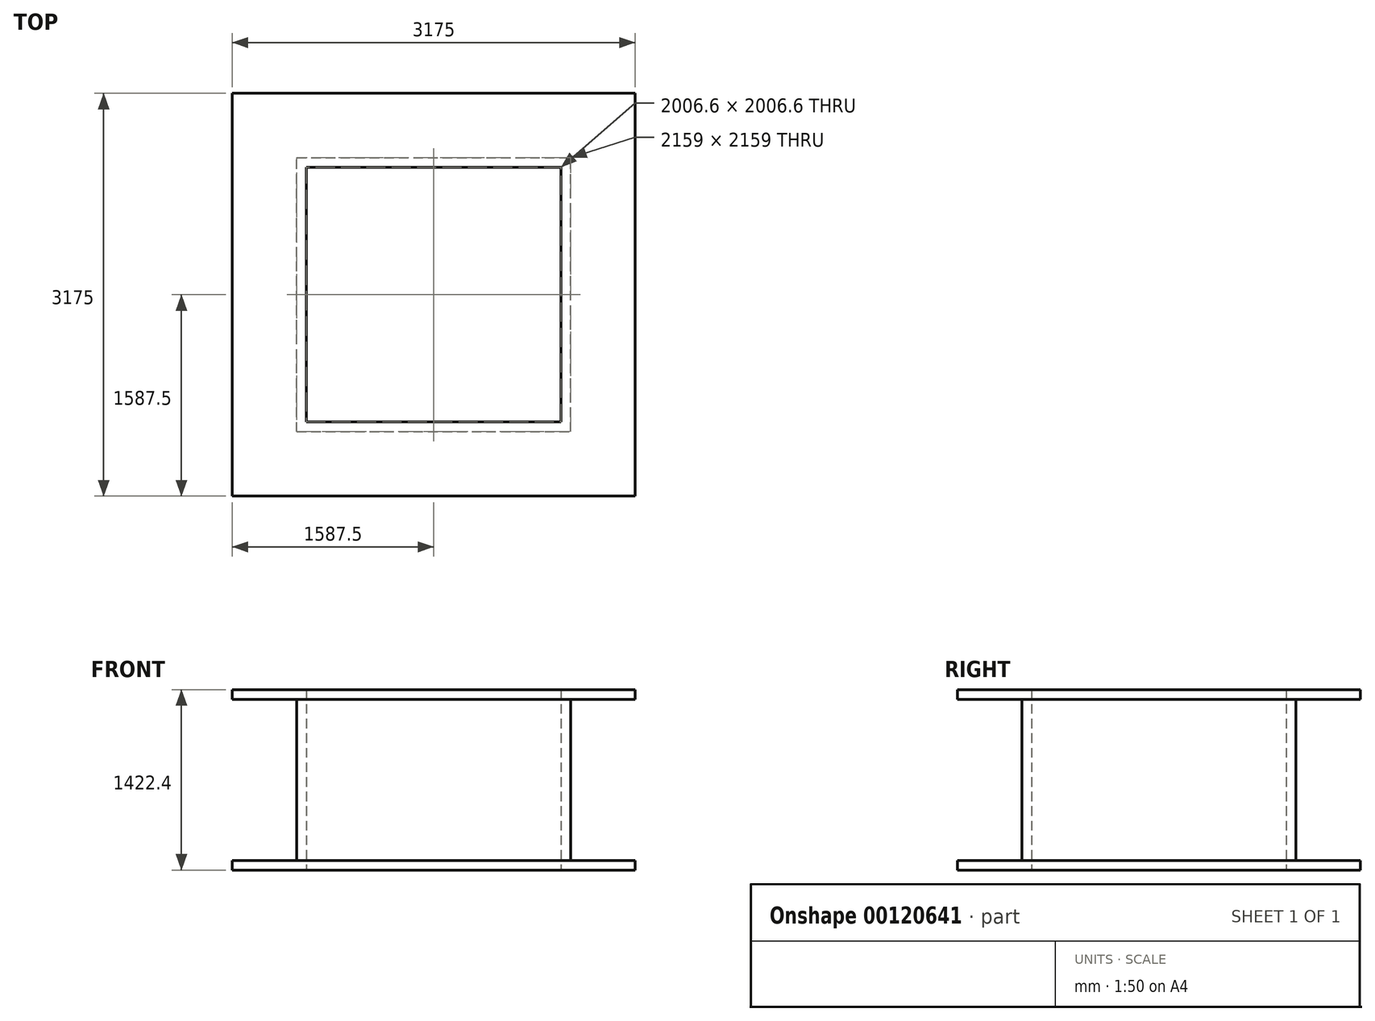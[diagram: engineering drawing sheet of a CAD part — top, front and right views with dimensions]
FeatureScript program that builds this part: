
annotation { "Feature Type Name" : "Feature", "Feature Type Description" : "" }
export const myFeature = defineFeature(function(context is Context, id is Id, definition is map)
    precondition{}
    {
        {
            var Q0;
            Q0=qCreatedBy(makeId("Top.planeOp"),FACE);
            var sketch = newSketch(context, id + "F0", { "sketchPlane" : qUnion([Q0])});
            skLineSegment(sketch, "E0.bottom", {"start": v(0, 0) * mm, "end": v(2159, 0) * mm});
            skLineSegment(sketch, "E0.top", {"start": v(0, 2159) * mm, "end": v(2159, 2159) * mm});
            skLineSegment(sketch, "E0.left", {"start": v(0, 0) * mm, "end": v(0, 2159) * mm});
            skLineSegment(sketch, "E0.right", {"start": v(2159, 0) * mm, "end": v(2159, 2159) * mm});
            skLineSegment(sketch, "E1.bottom", {"start": v(76.2, 2082.8) * mm, "end": v(2082.8, 2082.8) * mm});
            skLineSegment(sketch, "E1.top", {"start": v(76.2, 76.2) * mm, "end": v(2082.8, 76.2) * mm});
            skLineSegment(sketch, "E1.left", {"start": v(76.2, 2082.8) * mm, "end": v(76.2, 76.2) * mm});
            skLineSegment(sketch, "E1.right", {"start": v(2082.8, 2082.8) * mm, "end": v(2082.8, 76.2) * mm});
            skSolve(sketch);
        }
        {
            var Q0;
            Q0=qSketchRegion(id+"F0",true);
            extrude(context, id + "F1", {"entities" : qUnion([Q0]), "depth" : 1270 * mm});
        }
        {
            var Q0;
            Q0=makeQuery(id+"F1.opExtrude","CAP_FACE",FACE,{"disambiguationData":[OSD([sQuery(id+"F0.wireOp",EDGE,"E0.bottom"),sQuery(id+"F0.wireOp",EDGE,"E0.top"),sQuery(id+"F0.wireOp",EDGE,"E0.left"),sQuery(id+"F0.wireOp",EDGE,"E0.right"),sQuery(id+"F0.wireOp",EDGE,"E1.bottom"),sQuery(id+"F0.wireOp",EDGE,"E1.top"),sQuery(id+"F0.wireOp",EDGE,"E1.left"),sQuery(id+"F0.wireOp",EDGE,"E1.right")])],"isStart":false});
            var sketch = newSketch(context, id + "F2", { "sketchPlane" : qUnion([Q0])});
            skLineSegment(sketch, "E2.bottom", {"start": v(-508, -508) * mm, "end": v(2667, -508) * mm});
            skLineSegment(sketch, "E2.top", {"start": v(-508, 2667) * mm, "end": v(2667, 2667) * mm});
            skLineSegment(sketch, "E2.left", {"start": v(-508, -508) * mm, "end": v(-508, 2667) * mm});
            skLineSegment(sketch, "E2.right", {"start": v(2667, -508) * mm, "end": v(2667, 2667) * mm});
            skLineSegment(sketch, "E3.bottom", {"start": v(76.2, 2082.8) * mm, "end": v(2082.8, 2082.8) * mm});
            skLineSegment(sketch, "E3.top", {"start": v(76.2, 76.2) * mm, "end": v(2082.8, 76.2) * mm});
            skLineSegment(sketch, "E3.left", {"start": v(76.2, 2082.8) * mm, "end": v(76.2, 76.2) * mm});
            skLineSegment(sketch, "E3.right", {"start": v(2082.8, 2082.8) * mm, "end": v(2082.8, 76.2) * mm});
            skSolve(sketch);
        }
        {
            var Q0;
            Q0=qSketchRegion(id+"F2",true);
            extrude(context, id + "F3", {"entities" : qUnion([Q0]), "operationType" : NewBodyOperationType.ADD, "depth" : 76.2 * mm});
        }
        {
            var Q0;
            Q0=makeQuery(id+"F1.opExtrude","CAP_FACE",FACE,{"disambiguationData":[OSD([sQuery(id+"F0.wireOp",EDGE,"E0.bottom"),sQuery(id+"F0.wireOp",EDGE,"E0.top"),sQuery(id+"F0.wireOp",EDGE,"E0.left"),sQuery(id+"F0.wireOp",EDGE,"E0.right"),sQuery(id+"F0.wireOp",EDGE,"E1.bottom"),sQuery(id+"F0.wireOp",EDGE,"E1.top"),sQuery(id+"F0.wireOp",EDGE,"E1.left"),sQuery(id+"F0.wireOp",EDGE,"E1.right")])],"isStart":true});
            var sketch = newSketch(context, id + "F4", { "sketchPlane" : qUnion([Q0])});
            skLineSegment(sketch, "E4.bottom", {"start": v(76.2, -76.2) * mm, "end": v(2082.8, -76.2) * mm});
            skLineSegment(sketch, "E4.top", {"start": v(76.2, -2082.8) * mm, "end": v(2082.8, -2082.8) * mm});
            skLineSegment(sketch, "E4.left", {"start": v(76.2, -76.2) * mm, "end": v(76.2, -2082.8) * mm});
            skLineSegment(sketch, "E4.right", {"start": v(2082.8, -76.2) * mm, "end": v(2082.8, -2082.8) * mm});
            skLineSegment(sketch, "E5.bottom", {"start": v(-508, 508) * mm, "end": v(2667, 508) * mm});
            skLineSegment(sketch, "E5.top", {"start": v(-508, -2667) * mm, "end": v(2667, -2667) * mm});
            skLineSegment(sketch, "E5.left", {"start": v(-508, 508) * mm, "end": v(-508, -2667) * mm});
            skLineSegment(sketch, "E5.right", {"start": v(2667, 508) * mm, "end": v(2667, -2667) * mm});
            skSolve(sketch);
        }
        {
            var Q0;
            Q0=qSketchRegion(id+"F4",true);
            extrude(context, id + "F5", {"entities" : qUnion([Q0]), "operationType" : NewBodyOperationType.ADD, "depth" : 76.2 * mm});
        }
    });
